# Revit family: Urinal_Touchless-Wall_Mount-KOHLER-Portico-K-30897T_1
name_source: partatom
category: Plumbing Fixtures
units: mm (PartAtom-declared; Revit-internal decimal feet)

## family parameters
Cut with Voids When Loaded = No
Host = Face
OmniClass Number = 23.31.21.00
OmniClass Title = Urinals
Part Type = Normal
Room Calculation Point = No
Round Connector Dimension = Use Diameter
Shared = No

## types (5) — shared parameters
ADA Compliant = No
Assembly Code = D2010200
CW Connection = Yes
Cold Water Inlet = Cold Water Inlet
Date Modified = 07/28/2023
Default Elevation = 0"
Flow Rate = 0 GPM
HW Connection = No
Height = 26 13/16"
Hot Water Inlet = Hot Water Inlet
Length = 14 3/16"
Manufacturer = Kohler Co.
Master Format 2014 = 22 41 13.16
Master Format 2014 Name = Residential Urinals
Material = Vitreous China
Pressure = 0.00 psi
Product Name = Portico
URL = http://www.kohler.com.cn
Vent Connection = No
Waste Connection = Yes
Waste Water Outlet = Waste Water Outlet
WaterSense Certified = No
Width = 15 1/4"

## per-type parameters (varying)
| type | Description | Finish | Flush Rate- GPF | Flush Rate- LPF | Model | Type |
| 2.5 LPF, 0-White | Decorative With Touchless Urinal 2.5L | Kohler-Vitreous_China-0-White | 0.66 GPF | 2.5 LPF | K-30897T-0 | 5 |
| 0.5 LPF, XY, 0-White | Global Decorative With Touchless Urinal 0.5L | Kohler-Vitreous_China-0-White | 0.125 GPF | 0.5 LPF | K-30897T-XY-0 | 1 |
| 0.5 LPF, Y, 0-White | Global Decorative With Touchless Urinal 0.5L | Kohler-Vitreous_China-0-White | 0.125 GPF | 0.5 LPF | K-30897T-Y-0 | 3 |
| 0.5 LPF, Y, 7-Black Black | Global Decorative With Touchless Urinal 0.5L | Kohler-Vitreous_China-7-Black_Black | 0.125 GPF | 0.5 LPF | K-30897T-Y-7 | 2 |
| 2.5 LPF, 7-Black Black | Decorative With Touchless Urinal 2.5L | Kohler-Vitreous_China-7-Black_Black | 0.66 GPF | 2.5 LPF | K-30897T-7 | 4 |

## geometry (parser evidence)
native form markers: Sweep x4
no freeform markers — native parametric forms only
